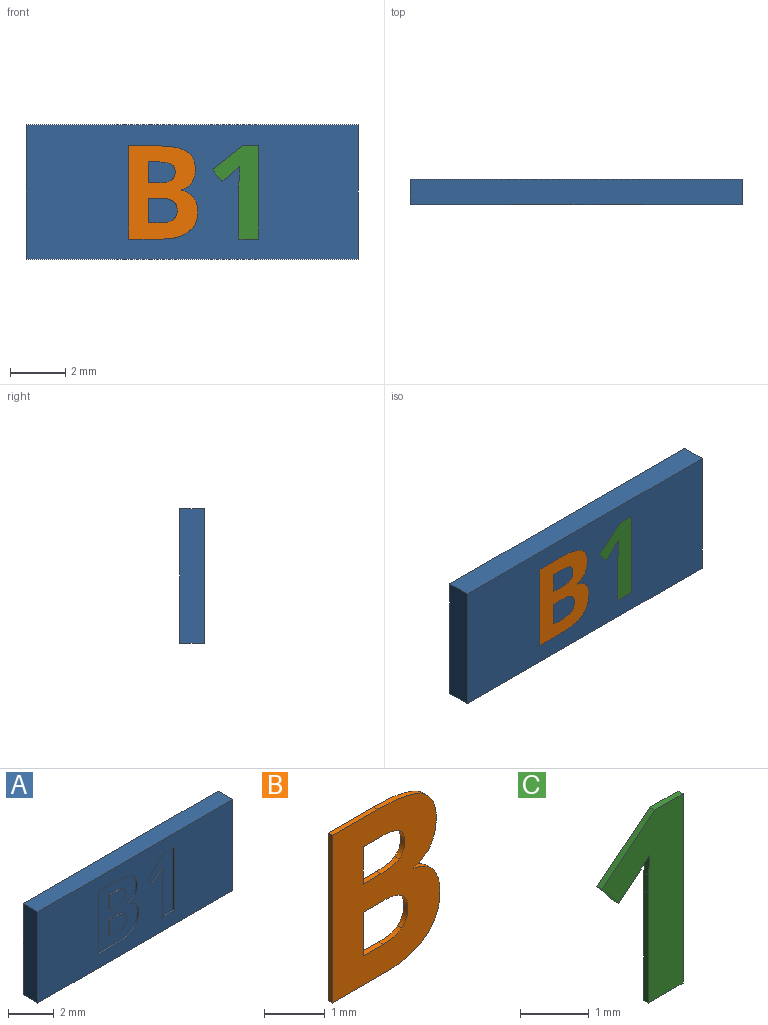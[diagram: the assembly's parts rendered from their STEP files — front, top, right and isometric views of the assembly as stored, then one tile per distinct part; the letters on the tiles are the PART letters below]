
ASSEMBLY  parts=3 mates=2
PART A: 45 faces, bbox 12x0.9x4.9 mm
  f0: plane 12x4.85mm, normal (0,-1,0), area 47.6mm2, adj f1,f2,f3,f4,f6,f7,f8,f9
  f1: plane 12x0.9mm, normal (0,0,-1), area 10.8mm2, adj f0,f2,f4,f5
  f2: plane 4.85x0.9mm, normal (1,0,0), area 4.4mm2, adj f0,f1,f3,f5
  f3: plane 12x0.9mm, normal (0,0,1), area 10.8mm2, adj f0,f2,f4,f5
  f4: plane 4.85x0.9mm, normal (-1,0,0), area 4.4mm2, adj f0,f1,f3,f5
  f5: plane 12x4.85mm, normal (0,1,0), area 58.2mm2, adj f1,f2,f3,f4
  f6: plane 3.37x0.1mm, normal (1,0,0), area 0.3mm2, adj f0,f7,f30,f31
  f7: plane 1.26x0.1mm, normal (0,0,1), area 0.1mm2, adj f0,f6,f8,f31
  f8: extruded ~0.91x0.26mm, area 0.1mm2, adj f0,f7,f9,f31
  f9: extruded ~0.72x0.33mm, area 0.1mm2, adj f0,f8,f10,f31
  f10: extruded ~0.52x0.14mm, area 0.1mm2, adj f0,f9,f11,f31
  f11: extruded ~0.46x0.27mm, area 0.1mm2, adj f0,f10,f12,f31
  f12: plane 0.1x0.02mm, normal (-1,0,0), area 0mm2, adj f0,f11,f13,f31
  f13: extruded ~0.38x0.23mm, area 0mm2, adj f0,f12,f14,f31
  f14: extruded ~0.5x0.14mm, area 0.1mm2, adj f0,f13,f15,f31
  f15: extruded ~0.65x0.32mm, area 0.1mm2, adj f0,f14,f16,f31
  f16: extruded ~1.04x0.2mm, area 0.1mm2, adj f0,f15,f30,f31
  f17: plane 0.75x0.1mm, normal (-1,0,0), area 0.1mm2, adj f18,f28,f31,f33
  f18: plane 0.38x0.1mm, normal (0,0,1), area 0mm2, adj f17,f19,f31,f33
  f19: extruded ~0.45x0.1mm, area 0mm2, adj f18,f20,f31,f33
  f20: extruded ~0.28x0.14mm, area 0mm2, adj f19,f21,f31,f33
  f21: extruded ~0.3x0.13mm, area 0mm2, adj f20,f22,f31,f33
  f22: extruded ~0.42x0.1mm, area 0mm2, adj f21,f28,f31,f33
  f23: plane 0.44x0.1mm, normal (0,0,1), area 0mm2, adj f24,f29,f31,f32
  f24: extruded ~0.6x0.42mm, area 0.1mm2, adj f23,f25,f31,f32
  f25: extruded ~0.35x0.14mm, area 0mm2, adj f24,f26,f31,f32
  f26: extruded ~0.44x0.11mm, area 0mm2, adj f25,f27,f31,f32
  f27: plane 0.47x0.1mm, normal (0,0,-1), area 0mm2, adj f26,f29,f31,f32
  f28: plane 0.41x0.1mm, normal (0,0,-1), area 0mm2, adj f17,f22,f31,f33
  f29: plane 0.88x0.1mm, normal (-1,0,0), area 0.1mm2, adj f23,f27,f31,f32
  f30: plane 1.05x0.1mm, normal (0,0,-1), area 0.1mm2, adj f0,f6,f16,f31
  f31: plane 3.37x2.5mm, normal (0,-1,0), area 6.2mm2, adj f6,f7,f8,f9,f10,f11,f12,f13
  f32: plane 1.04x0.88mm, normal (0,-1,0), area 0.8mm2, adj f23,f24,f25,f26,f27,f29
  f33: plane 0.97x0.75mm, normal (0,-1,0), area 0.7mm2, adj f17,f18,f19,f20,f21,f22,f28
  f34: plane 3.37x0.1mm, normal (-1,0,0), area 0.3mm2, adj f0,f35,f43,f44
  f35: plane 0.59x0.1mm, normal (0,0,-1), area 0.1mm2, adj f0,f34,f36,f44
  f36: plane 1.09x0.86mm, normal (0.62,0,-0.78), area 0.1mm2, adj f0,f35,f37,f44
  f37: plane 0.43x0.34mm, normal (0.78,0,0.63), area 0.1mm2, adj f0,f36,f38,f44
  f38: plane 0.39x0.31mm, normal (-0.63,0,0.78), area 0mm2, adj f0,f37,f39,f44
  f39: extruded ~0.25x0.23mm, area 0mm2, adj f0,f38,f40,f44
  f40: plane 0.35x0.1mm, normal (1,0,-0.03), area 0mm2, adj f0,f39,f41,f44
  f41: plane 0.32x0.1mm, normal (1,0,-0.02), area 0mm2, adj f0,f40,f42,f44
  f42: plane 1.95x0.1mm, normal (1,0,0), area 0.2mm2, adj f0,f41,f43,f44
  f43: plane 0.71x0.1mm, normal (0,0,1), area 0.1mm2, adj f0,f34,f42,f44
  f44: plane 3.37x1.67mm, normal (0,-1,0), area 2.9mm2, adj f34,f35,f36,f37,f38,f39,f40,f41
PART B: 27 faces, bbox 2.5x0.1x3.4 mm
  f0: plane 3.37x2.5mm, normal (0,-1,0), area 6.2mm2, adj f1,f2,f3,f4,f5,f6,f7,f8
  f1: plane 1.26x0.1mm, normal (0,0,-1), area 0.1mm2, adj f0,f2,f17,f19
  f2: extruded ~0.91x0.26mm, area 0.1mm2, adj f0,f1,f3,f17
  f3: extruded ~0.72x0.33mm, area 0.1mm2, adj f0,f2,f4,f17
  f4: extruded ~0.52x0.14mm, area 0.1mm2, adj f0,f3,f5,f17
  f5: extruded ~0.46x0.27mm, area 0.1mm2, adj f0,f4,f6,f17
  f6: plane 0.1x0.02mm, normal (1,0,0), area 0mm2, adj f0,f5,f7,f17
  f7: extruded ~0.38x0.23mm, area 0mm2, adj f0,f6,f8,f17
  f8: extruded ~0.5x0.14mm, area 0.1mm2, adj f0,f7,f9,f17
  f9: extruded ~0.65x0.32mm, area 0.1mm2, adj f0,f8,f17,f18
  f10: plane 0.38x0.1mm, normal (0,0,-1), area 0mm2, adj f0,f11,f17,f25
  f11: extruded ~0.45x0.1mm, area 0mm2, adj f0,f10,f12,f17
  f12: extruded ~0.28x0.14mm, area 0mm2, adj f0,f11,f13,f17
  f13: extruded ~0.3x0.13mm, area 0mm2, adj f0,f12,f17,f24
  f14: extruded ~0.6x0.42mm, area 0.1mm2, adj f0,f15,f17,f22
  f15: extruded ~0.35x0.14mm, area 0mm2, adj f0,f14,f16,f17
  f16: extruded ~0.44x0.11mm, area 0mm2, adj f0,f15,f17,f21
  f17: plane 3.37x2.5mm, normal (0,1,0), area 6.2mm2, adj f1,f2,f3,f4,f5,f6,f7,f8
  f18: extruded ~1.04x0.2mm, area 0.1mm2, adj f0,f9,f17,f20
  f19: plane 3.37x0.1mm, normal (-1,0,0), area 0.3mm2, adj f0,f1,f17,f20
  f20: plane 1.05x0.1mm, normal (0,0,1), area 0.1mm2, adj f0,f17,f18,f19
  f21: plane 0.47x0.1mm, normal (0,0,1), area 0mm2, adj f0,f16,f17,f23
  f22: plane 0.44x0.1mm, normal (0,0,-1), area 0mm2, adj f0,f14,f17,f23
  f23: plane 0.88x0.1mm, normal (1,0,0), area 0.1mm2, adj f0,f17,f21,f22
  f24: extruded ~0.42x0.1mm, area 0mm2, adj f0,f13,f17,f26
  f25: plane 0.75x0.1mm, normal (1,0,0), area 0.1mm2, adj f0,f10,f17,f26
  f26: plane 0.41x0.1mm, normal (0,0,1), area 0mm2, adj f0,f17,f24,f25
PART C: 12 faces, bbox 1.7x0.1x3.4 mm
  f0: plane 3.37x1.67mm, normal (0,-1,0), area 2.9mm2, adj f1,f2,f3,f4,f5,f6,f7,f9
  f1: plane 0.59x0.1mm, normal (0,0,1), area 0.1mm2, adj f0,f2,f8,f10
  f2: plane 1.09x0.86mm, normal (-0.62,0,0.78), area 0.1mm2, adj f0,f1,f3,f8
  f3: plane 0.43x0.34mm, normal (-0.78,0,-0.63), area 0.1mm2, adj f0,f2,f4,f8
  f4: plane 0.39x0.31mm, normal (0.63,0,-0.78), area 0mm2, adj f0,f3,f5,f8
  f5: extruded ~0.25x0.23mm, area 0mm2, adj f0,f4,f6,f8
  f6: plane 0.35x0.1mm, normal (-1,0,0.03), area 0mm2, adj f0,f5,f7,f8
  f7: plane 0.32x0.1mm, normal (-1,0,0.02), area 0mm2, adj f0,f6,f8,f9
  f8: plane 3.37x1.67mm, normal (0,1,0), area 2.9mm2, adj f1,f2,f3,f4,f5,f6,f7,f9
  f9: plane 1.95x0.1mm, normal (-1,0,0), area 0.2mm2, adj f0,f7,f8,f11
  f10: plane 3.37x0.1mm, normal (1,0,0), area 0.3mm2, adj f0,f1,f8,f11
  f11: plane 0.71x0.1mm, normal (0,0,-1), area 0.1mm2, adj f0,f8,f9,f10
PLACE A t=(0.03,0.45,0.02)mm
PLACE B t=(0.03,0.45,0.02)mm
PLACE C t=(0.05,0.35,0.02)mm
MATE fastened C.f0 <-> A.f0  axis (0,-1,0) through (1.73,-0.45,-1.68)mm
MATE fastened B.f0 <-> A.f0  axis (0,-1,0) through (-2.26,-0.45,-1.68)mm
